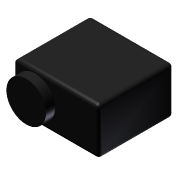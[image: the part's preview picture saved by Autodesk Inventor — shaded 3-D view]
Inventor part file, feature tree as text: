
AUTODESK INVENTOR PART (.ipt)
format: ipt  version: 2012 (Build 160160000, 160)  size: 123,904 bytes
history: native  units: mm
features: sketch x3, extrude x3, fillet x1
ambient origin geometry x8: Origin, YZ Plane, XZ Plane, XY Plane, X Axis, Y Axis, Z Axis, Center Point
bodies: Solid1 (feature_tree)
feature tree (7):
  sketch  "Sketch1"  dims[d2=11.0mm d3=11.0mm d4=5.0mm d5=26.0mm d6=0.0mm]
  extrude  "Extrusion1"  Depth=26.0mm TaperAngle=0.0deg
  extrude  "Extrusion2"  Depth=21.0mm
  extrude  "Extrusion3"  Depth=11.0mm
  fillet  "Fillet1"  Radius=22.0mm
  sketch  "Sketch2"  dims[d7=11.0mm d8=21.0mm]
  sketch  "Sketch3"  dims[d9=1.0mm d10=0.0mm d11=11.0mm d12=22.0mm d13=5.0mm d14=0.0mm d15=2.0mm]
